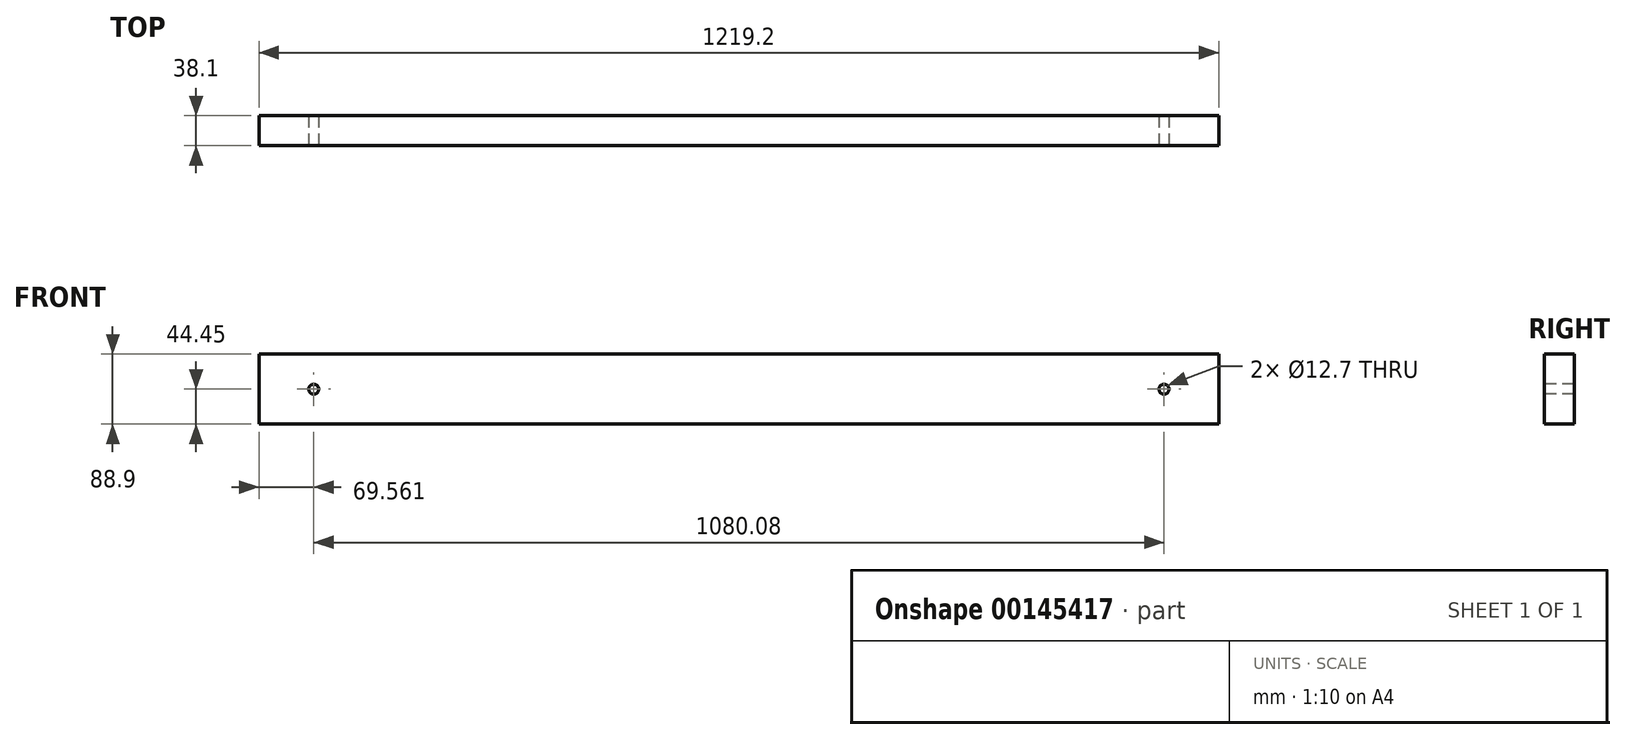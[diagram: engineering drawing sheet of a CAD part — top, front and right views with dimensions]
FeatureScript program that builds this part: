
annotation { "Feature Type Name" : "Feature", "Feature Type Description" : "" }
export const myFeature = defineFeature(function(context is Context, id is Id, definition is map)
    precondition{}
    {
        {
            var Q0;
            Q0=qCreatedBy(makeId("Front.planeOp"),FACE);
            var sketch = newSketch(context, id + "F0", { "sketchPlane" : qUnion([Q0])});
            skLineSegment(sketch, "E0.bottom", {"start": v(-609.6, 44.45) * mm, "end": v(609.6, 44.45) * mm});
            skLineSegment(sketch, "E0.top", {"start": v(-609.6, -44.45) * mm, "end": v(609.6, -44.45) * mm});
            skLineSegment(sketch, "E0.left", {"start": v(-609.6, 44.45) * mm, "end": v(-609.6, -44.45) * mm});
            skLineSegment(sketch, "E0.right", {"start": v(609.6, 44.45) * mm, "end": v(609.6, -44.45) * mm});
            skPoint(sketch, "E0.middle", {"position": v(0, 0) * mm});
            skPoint(sketch, "E1", {"position": v(-540.04, 0) * mm});
            skPoint(sketch, "E2", {"position": v(540.04, 0) * mm});
            skSolve(sketch);
        }
        {
            var Q0;
            Q0=makeQuery(id+"F0.imprint","IMPRINT",FACE,{"disambiguationData":[TD([[makeQuery(id+"F0.imprint","IMPRINT",EDGE,{"derivedFrom":sQuery(id+"F0.wireOp",EDGE,"E0.bottom")}),-1.0]])]});
            extrude(context, id + "F1", {"entities" : qUnion([Q0]), "oppositeDirection" : true, "depth" : 38.1 * mm});
        }
        {
            var Q0;
            Q0=sQuery(id+"F0.wireOp",VERTEX,"E1");
            var Q1;
            Q1=sQuery(id+"F0.wireOp",VERTEX,"E2");
            var Q2;
            Q2=makeQuery(id+"F1.opExtrude","SWEPT_BODY",BODY,{"disambiguationData":[OSD([sQuery(id+"F0.wireOp",EDGE,"E0.bottom"),sQuery(id+"F0.wireOp",EDGE,"E0.top"),sQuery(id+"F0.wireOp",EDGE,"E0.left"),sQuery(id+"F0.wireOp",EDGE,"E0.right")])]});
            hole(context, id + "F2", {"style" : HoleStyle.SIMPLE, "endStyle" : HoleEndStyle.BLIND, "holeDiameter" : 12.7 * mm, "holeDepth" : 609.6 * mm, "startFromSketch" : true, "locations" : qUnion([Q0, Q1]), "scope" : qUnion([Q2])});
        }
    });
